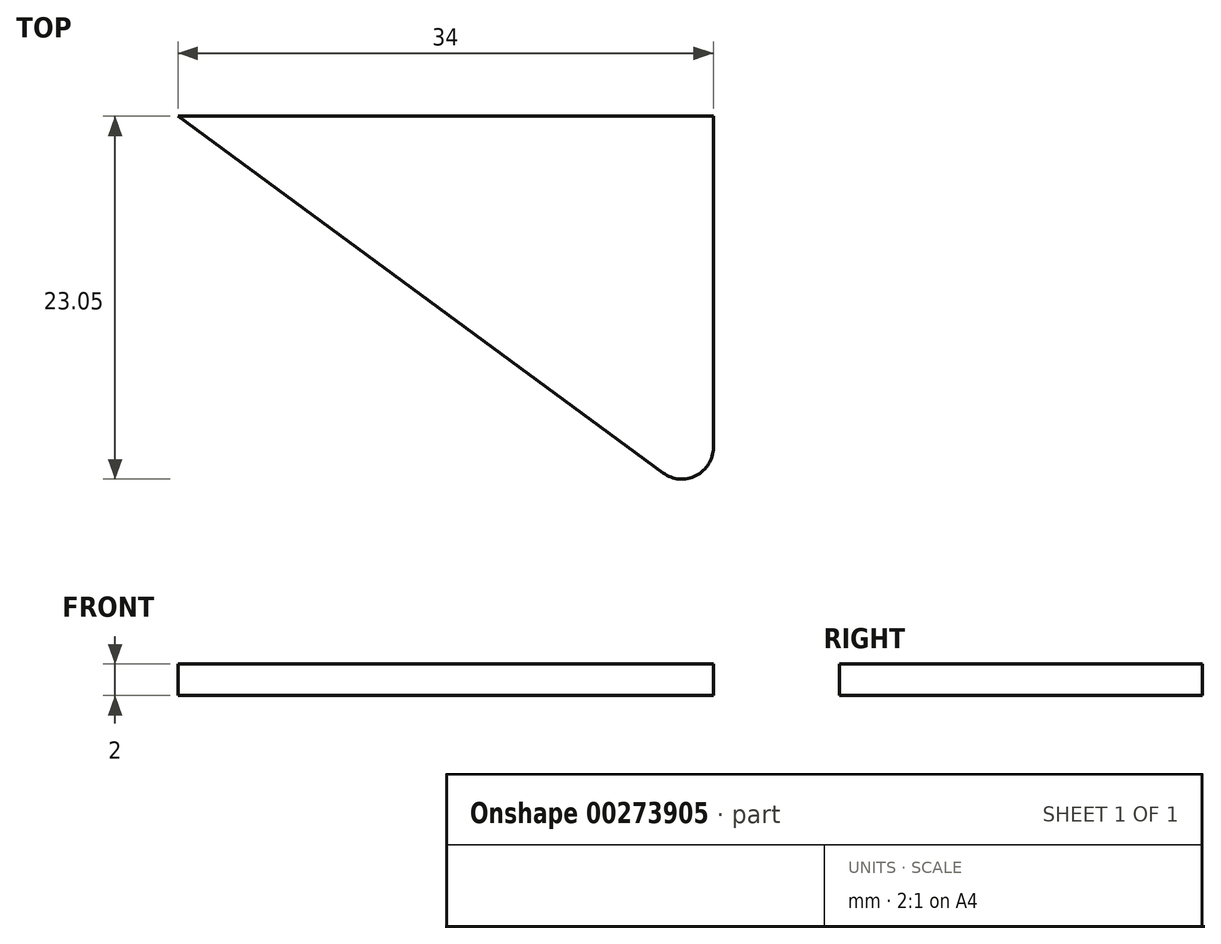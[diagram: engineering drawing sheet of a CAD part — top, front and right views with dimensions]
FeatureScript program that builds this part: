
annotation { "Feature Type Name" : "Feature", "Feature Type Description" : "" }
export const myFeature = defineFeature(function(context is Context, id is Id, definition is map)
    precondition{}
    {
        {
            var Q0;
            Q0=qCreatedBy(makeId("Top.planeOp"),FACE);
            var sketch = newSketch(context, id + "F0", { "sketchPlane" : qUnion([Q0])});
            skLineSegment(sketch, "E0", {"start": v(0, 0) * mm, "end": v(34, 0) * mm});
            skLineSegment(sketch, "E1", {"start": v(34, 0) * mm, "end": v(34, -21.05) * mm});
            skLineSegment(sketch, "E2", {"start": v(30.82, -22.66) * mm, "end": v(0, 0) * mm});
            skPoint(sketch, "E3.visualSharp", {"position": v(34, -25) * mm});
            skArc(sketch, "E3.filletArc", {"start": v(30.82, -22.66) * mm, "mid": v(32.9, -22.83) * mm, "end": v(34, -21.05) * mm});
            skSolve(sketch);
        }
        {
            var Q0;
            Q0=makeQuery(id+"F0.imprint","IMPRINT",FACE,{"disambiguationData":[TD([[makeQuery(id+"F0.imprint","IMPRINT",EDGE,{"derivedFrom":sQuery(id+"F0.wireOp",EDGE,"E0")}),-1.0]])]});
            extrude(context, id + "F1", {"entities" : qUnion([Q0]), "depth" : 2 * mm});
        }
    });
